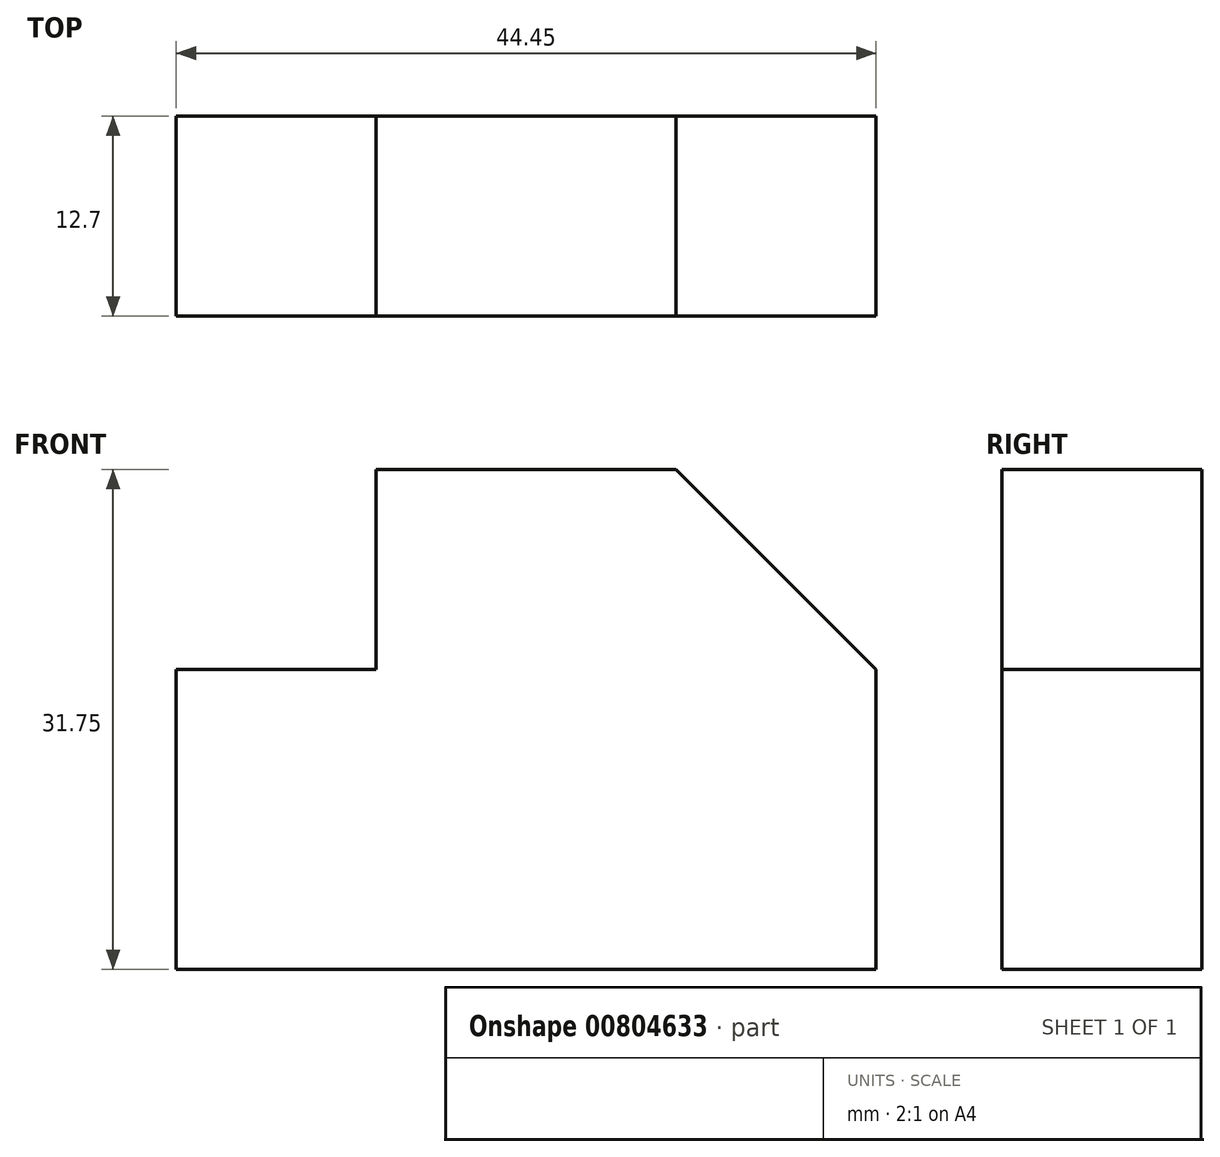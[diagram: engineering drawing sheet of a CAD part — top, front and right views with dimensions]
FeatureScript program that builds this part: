
annotation { "Feature Type Name" : "Feature", "Feature Type Description" : "" }
export const myFeature = defineFeature(function(context is Context, id is Id, definition is map)
    precondition{}
    {
        {
            var Q0;
            Q0=qCreatedBy(makeId("Front.planeOp"),FACE);
            var sketch = newSketch(context, id + "F0", { "sketchPlane" : qUnion([Q0])});
            skLineSegment(sketch, "E0", {"start": v(0, 0) * mm, "end": v(44.45, 0) * mm});
            skLineSegment(sketch, "E1", {"start": v(44.45, 0) * mm, "end": v(44.45, 19.05) * mm});
            skLineSegment(sketch, "E2", {"start": v(0, 0) * mm, "end": v(0, 19.05) * mm});
            skLineSegment(sketch, "E3", {"start": v(0, 19.05) * mm, "end": v(12.7, 19.05) * mm});
            skLineSegment(sketch, "E4", {"start": v(12.7, 19.05) * mm, "end": v(12.7, 31.75) * mm});
            skLineSegment(sketch, "E5", {"start": v(12.7, 31.75) * mm, "end": v(31.75, 31.75) * mm});
            skLineSegment(sketch, "E6", {"start": v(31.75, 31.75) * mm, "end": v(44.45, 19.05) * mm});
            skSolve(sketch);
        }
        {
            var Q0;
            Q0 = qSketchRegion(id + "F0", true);
            extrude(context, id + "F1", {"entities" : qUnion([Q0]), "depth" : 12.7 * mm, "offsetDistance" : 25.4 * mm});
        }
    });
